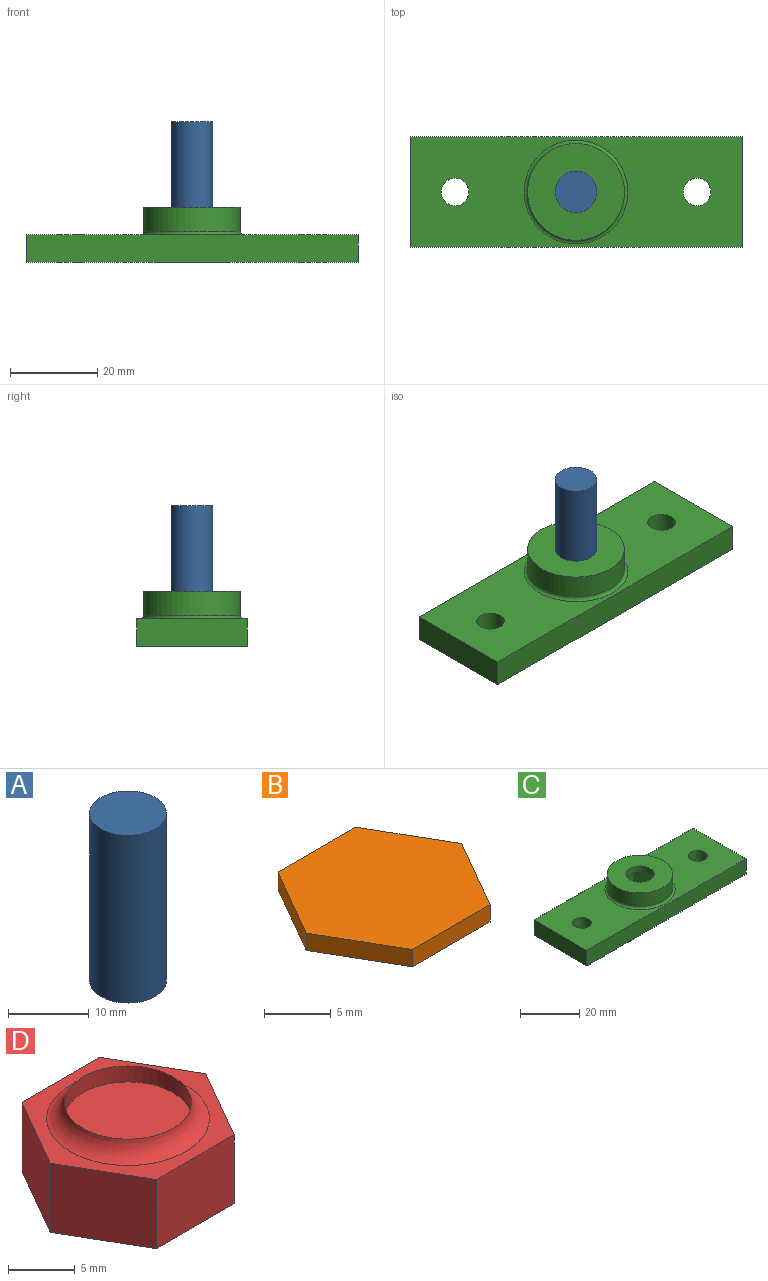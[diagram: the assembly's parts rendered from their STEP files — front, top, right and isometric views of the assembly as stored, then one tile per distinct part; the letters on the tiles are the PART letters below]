
ASSEMBLY  parts=4 mates=3
PART A: 3 faces, bbox 9.5x9.5x25.4 mm
  f0: cylinder r=4.76mm len=25.4mm, axis (0,0,-1), area 760.1mm2, adj f1,f2
  f1: plane 9.53x9.53mm, normal (0,0,1), area 71.3mm2, adj f0
  f2: plane 9.53x9.53mm, normal (0,0,-1), area 71.3mm2, adj f0
PART B: 8 faces, bbox 16.5x14.3x1.6 mm
  f0: plane 7.14x4.12mm, normal (0.87,-0.5,0), area 13.1mm2, adj f1,f5,f6,f7
  f1: plane 7.14x4.12mm, normal (0.87,0.5,0), area 13.1mm2, adj f0,f2,f6,f7
  f2: plane 8.25x1.59mm, normal (0,1,0), area 13.1mm2, adj f1,f3,f6,f7
  f3: plane 7.14x4.12mm, normal (-0.87,0.5,0), area 13.1mm2, adj f2,f4,f6,f7
  f4: plane 7.14x4.12mm, normal (-0.87,-0.5,0), area 13.1mm2, adj f3,f5,f6,f7
  f5: plane 8.25x1.59mm, normal (0,-1,0), area 13.1mm2, adj f0,f4,f6,f7
  f6: plane 16.5x14.29mm, normal (0,0,1), area 176.8mm2, adj f0,f1,f2,f3,f4,f5
  f7: plane 16.5x14.29mm, normal (0,0,-1), area 176.8mm2, adj f0,f1,f2,f3,f4,f5
PART C: 26 faces, bbox 76.2x25.8x12.7 mm
  f0: plane 76.2x25.4mm, normal (0,0,-1), area 1686mm2, adj f2,f3,f4,f5,f9,f10,f11,f12
  f1: cylinder r=4.76mm len=9.53mm, axis (0,0,1), area 71.4mm2, adj f8,f22
  f2: plane 76.2x6.35mm, normal (0,1,0), area 483.9mm2, adj f0,f3,f5,f6
  f3: plane 25.4x6.35mm, normal (-1,0,0), area 161.3mm2, adj f0,f2,f4,f6
  f4: plane 76.2x6.35mm, normal (0,-1,0), area 483.9mm2, adj f0,f3,f5,f6
  f5: plane 25.4x6.35mm, normal (1,0,0), area 161.3mm2, adj f0,f2,f4,f6
  f6: plane 76.2x25.4mm, normal (0,0,1), area 1427.3mm2, adj f2,f3,f4,f5,f23,f24,f25
  f7: cylinder r=11.11mm len=22.23mm, axis (0,0,-1), area 388.4mm2, adj f8,f23
  f8: plane 22.23x22.23mm, normal (0,0,1), area 316.7mm2, adj f1,f7
  f9: plane 8.74x7.33mm, normal (-0.87,0.5,0), area 74mm2, adj f0,f10,f14,f19
  f10: plane 8.74x8.46mm, normal (0,1,0), area 74mm2, adj f0,f9,f11,f17
  f11: plane 8.74x7.33mm, normal (0.87,0.5,0), area 74mm2, adj f0,f10,f12,f16
  f12: plane 8.74x7.33mm, normal (0.87,-0.5,0), area 74mm2, adj f0,f11,f13,f18
  f13: plane 8.74x8.46mm, normal (0,-1,0), area 74mm2, adj f0,f12,f14,f20
  f14: plane 8.74x7.33mm, normal (-0.87,-0.5,0), area 74mm2, adj f0,f9,f13,f21
  f15: plane 15.11x13.09mm, normal (0,0,-1), area 51.5mm2, adj f16,f17,f18,f19,f20,f21,f22
  f16: cylinder r=0.79mm len=7.72mm, axis (-0.5,0.87,0), area 10.1mm2, adj f11,f15,f17,f18
  f17: cylinder r=0.79mm len=8.46mm, axis (-1,0,0), area 10.1mm2, adj f10,f15,f16,f19
  f18: cylinder r=0.79mm len=7.72mm, axis (0.5,0.87,0), area 10.1mm2, adj f12,f15,f16,f20
  f19: cylinder r=0.79mm len=7.72mm, axis (-0.5,-0.87,0), area 10.1mm2, adj f9,f15,f17,f21
  f20: cylinder r=0.79mm len=8.46mm, axis (1,0,0), area 10.1mm2, adj f13,f15,f18,f21
  f21: cylinder r=0.79mm len=7.72mm, axis (0.5,-0.87,0), area 10.1mm2, adj f14,f15,f19,f20
  f22: torus R=5.55mm, axis (0,0,-1), area 39.2mm2, adj f1,f15
  f23: torus R=11.9mm, axis (0,0,1), area 88.6mm2, adj f6,f7
  f24: cylinder r=3.17mm len=6.35mm, axis (0,0,1), area 126.7mm2, adj f0,f6
  f25: cylinder r=3.17mm len=6.35mm, axis (0,0,1), area 126.7mm2, adj f0,f6
PART D: 11 faces, bbox 16.5x14.3x8.1 mm
  f0: plane 7.14x6.35mm, normal (-0.87,0.5,0), area 52.4mm2, adj f1,f5,f6,f7
  f1: plane 7.14x6.35mm, normal (-0.87,-0.5,0), area 52.4mm2, adj f0,f2,f6,f7
  f2: plane 8.25x6.35mm, normal (0,-1,0), area 52.4mm2, adj f1,f3,f6,f7
  f3: plane 7.14x6.35mm, normal (0.87,-0.5,0), area 52.4mm2, adj f2,f4,f6,f7
  f4: plane 7.14x6.35mm, normal (0.87,0.5,0), area 52.4mm2, adj f3,f5,f6,f7
  f5: plane 8.25x6.35mm, normal (0,1,0), area 52.4mm2, adj f0,f4,f6,f7
  f6: plane 16.5x14.29mm, normal (0,0,-1), area 176.8mm2, adj f0,f1,f2,f3,f4,f5
  f7: plane 16.5x14.29mm, normal (0,0,1), area 59.1mm2, adj f0,f1,f2,f3,f4,f5,f9
  f8: cylinder r=4.77mm len=9.53mm, axis (0,0,-1), area 44mm2, adj f9,f10
  f9: torus R=6.53mm, axis (0,0,-1), area 70.5mm2, adj f7,f8
  f10: plane 9.53x9.53mm, normal (0,0,1), area 71.4mm2, adj f8
PLACE A t=(-34.58,-17.01,10.58)mm
PLACE B t=(-34.58,-17.01,3.64)mm
PLACE C t=(-72.68,-29.71,3.64)mm
PLACE D t=(-34.58,-17.01,13.17)mm
MATE planar C.f15 <-> D.f7  axis (0,0,-1) through (-42.14,-17.01,13.17)mm
MATE cylindrical C.f1 <-> A.f0  axis (0,0,1) through (-34.58,-17.01,16.34)mm
MATE planar B.f7 <-> C.f1  axis (0,0,-1) through (-34.58,-17.01,3.64)mm
